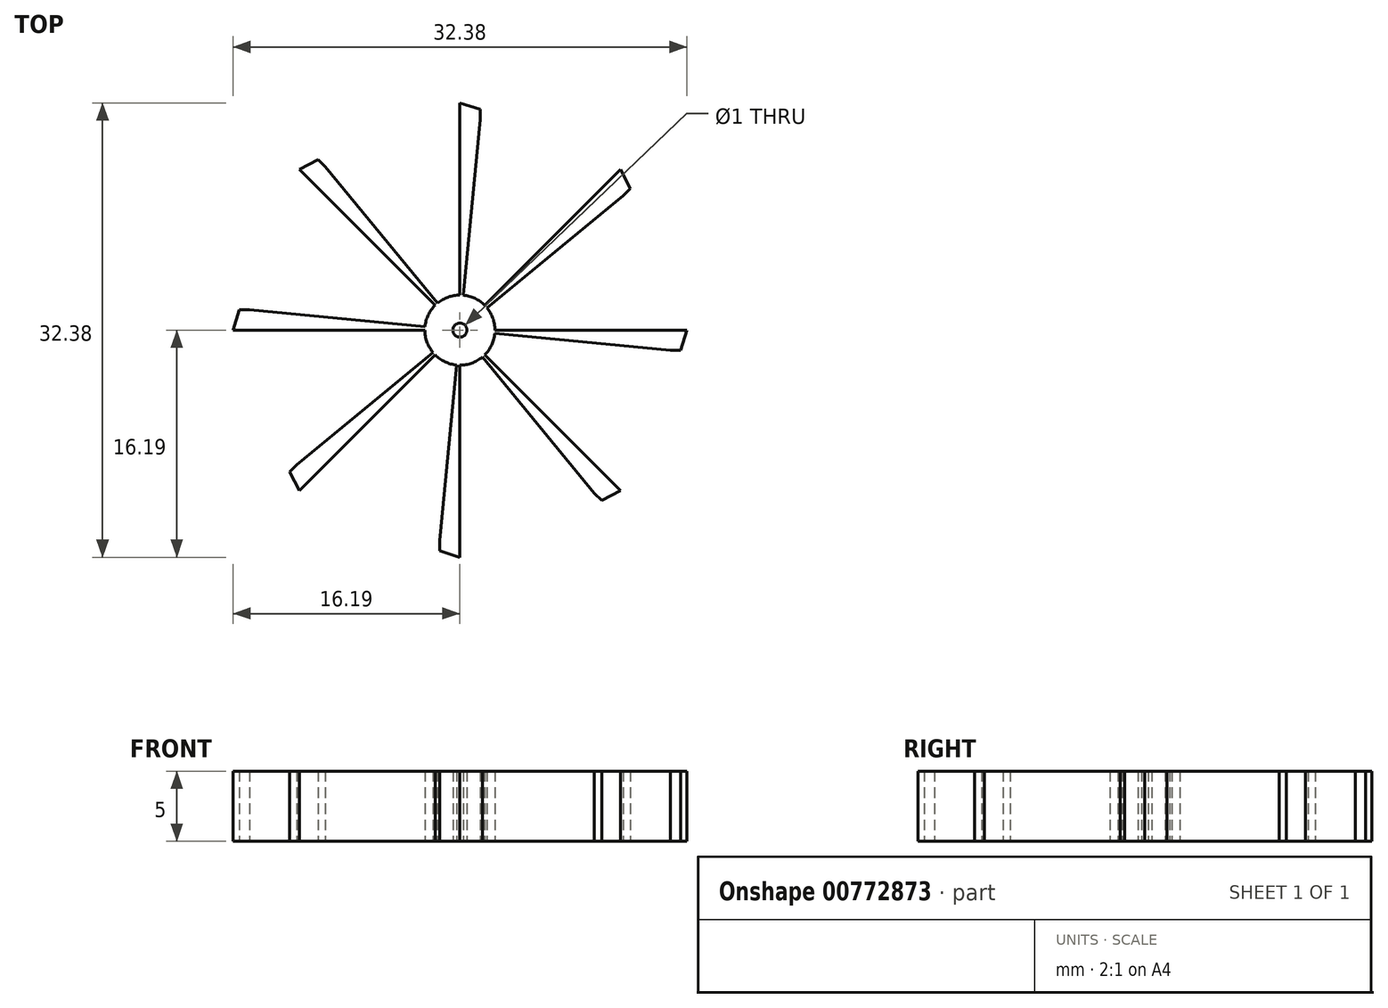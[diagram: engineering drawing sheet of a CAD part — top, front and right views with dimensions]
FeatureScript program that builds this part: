
annotation { "Feature Type Name" : "Feature", "Feature Type Description" : "" }
export const myFeature = defineFeature(function(context is Context, id is Id, definition is map)
    precondition{}
    {
        {
            var Q0;
            Q0=qCreatedBy(makeId("Top.planeOp"),FACE);
            var sketch = newSketch(context, id + "F0", { "sketchPlane" : qUnion([Q0])});
            skCircle(sketch, "E0", {"center": v(0, 0) * mm, "radius": 0.5 * mm});
            skCircle(sketch, "E1", {"center": v(0, 0) * mm, "radius": 2.5 * mm});
            skSolve(sketch);
        }
        {
            var Q0;
            Q0=makeQuery(id+"F0.imprint","IMPRINT",FACE,{"disambiguationData":[TD([[makeQuery(id+"F0.imprint","IMPRINT",EDGE,{"derivedFrom":sQuery(id+"F0.wireOp",EDGE,"E0")}),-1.0]])]});
            extrude(context, id + "F1", {"entities" : qUnion([Q0]), "depth" : 5 * mm, "offsetDistance" : 25 * mm});
        }
        {
            var Q0;
            Q0=qCreatedBy(makeId("Top.planeOp"),FACE);
            var sketch = newSketch(context, id + "F2", { "sketchPlane" : qUnion([Q0])});
            skLineSegment(sketch, "E2", {"start": v(0, 1.39) * mm, "end": v(0, 15) * mm});
            skLineSegment(sketch, "E3", {"start": v(0, 15) * mm, "end": v(1.44, 15) * mm, "construction": true});
            skLineSegment(sketch, "E4", {"start": v(1.44, 15) * mm, "end": v(0.13, 1.38) * mm});
            skLineSegment(sketch, "E5", {"start": v(0, 15) * mm, "end": v(0, 16.19) * mm});
            skLineSegment(sketch, "E6", {"start": v(0, 16.19) * mm, "end": v(1.44, 15.73) * mm});
            skLineSegment(sketch, "E7", {"start": v(1.44, 15.73) * mm, "end": v(1.44, 15) * mm});
            skLineSegment(sketch, "E8.1.0", {"start": v(-9.59, 11.63) * mm, "end": v(-0.88, 1.07) * mm});
            skLineSegment(sketch, "E8.1.1", {"start": v(-10.1, 12.14) * mm, "end": v(-9.59, 11.63) * mm});
            skLineSegment(sketch, "E8.1.2", {"start": v(-11.45, 11.45) * mm, "end": v(-10.1, 12.14) * mm});
            skLineSegment(sketch, "E8.1.3", {"start": v(-10.6, 10.6) * mm, "end": v(-11.45, 11.45) * mm});
            skLineSegment(sketch, "E8.1.4", {"start": v(-0.98, 0.98) * mm, "end": v(-10.6, 10.6) * mm});
            skLineSegment(sketch, "E8.2.0", {"start": v(-15, 1.44) * mm, "end": v(-1.38, 0.13) * mm});
            skLineSegment(sketch, "E8.2.1", {"start": v(-15.73, 1.44) * mm, "end": v(-15, 1.44) * mm});
            skLineSegment(sketch, "E8.2.2", {"start": v(-16.19, 0) * mm, "end": v(-15.73, 1.44) * mm});
            skLineSegment(sketch, "E8.2.3", {"start": v(-15, 0) * mm, "end": v(-16.19, 0) * mm});
            skLineSegment(sketch, "E8.2.4", {"start": v(-1.39, 0) * mm, "end": v(-15, 0) * mm});
            skLineSegment(sketch, "E8.3.0", {"start": v(-11.63, -9.59) * mm, "end": v(-1.07, -0.88) * mm});
            skLineSegment(sketch, "E8.3.1", {"start": v(-12.14, -10.1) * mm, "end": v(-11.63, -9.59) * mm});
            skLineSegment(sketch, "E8.3.2", {"start": v(-11.45, -11.45) * mm, "end": v(-12.14, -10.1) * mm});
            skLineSegment(sketch, "E8.3.3", {"start": v(-10.6, -10.6) * mm, "end": v(-11.45, -11.45) * mm});
            skLineSegment(sketch, "E8.3.4", {"start": v(-0.98, -0.98) * mm, "end": v(-10.6, -10.6) * mm});
            skLineSegment(sketch, "E8.4.0", {"start": v(-1.44, -15) * mm, "end": v(-0.13, -1.38) * mm});
            skLineSegment(sketch, "E8.4.1", {"start": v(-1.44, -15.73) * mm, "end": v(-1.44, -15) * mm});
            skLineSegment(sketch, "E8.4.2", {"start": v(0, -16.19) * mm, "end": v(-1.44, -15.73) * mm});
            skLineSegment(sketch, "E8.4.3", {"start": v(0, -15) * mm, "end": v(0, -16.19) * mm});
            skLineSegment(sketch, "E8.4.4", {"start": v(0, -1.39) * mm, "end": v(0, -15) * mm});
            skLineSegment(sketch, "E8.5.0", {"start": v(9.59, -11.63) * mm, "end": v(0.88, -1.07) * mm});
            skLineSegment(sketch, "E8.5.1", {"start": v(10.1, -12.14) * mm, "end": v(9.59, -11.63) * mm});
            skLineSegment(sketch, "E8.5.2", {"start": v(11.45, -11.45) * mm, "end": v(10.1, -12.14) * mm});
            skLineSegment(sketch, "E8.5.3", {"start": v(10.6, -10.6) * mm, "end": v(11.45, -11.45) * mm});
            skLineSegment(sketch, "E8.5.4", {"start": v(0.98, -0.98) * mm, "end": v(10.6, -10.6) * mm});
            skLineSegment(sketch, "E8.6.0", {"start": v(15, -1.44) * mm, "end": v(1.38, -0.13) * mm});
            skLineSegment(sketch, "E8.6.1", {"start": v(15.73, -1.44) * mm, "end": v(15, -1.44) * mm});
            skLineSegment(sketch, "E8.6.2", {"start": v(16.19, 0) * mm, "end": v(15.73, -1.44) * mm});
            skLineSegment(sketch, "E8.6.3", {"start": v(15, 0) * mm, "end": v(16.19, 0) * mm});
            skLineSegment(sketch, "E8.6.4", {"start": v(1.39, 0) * mm, "end": v(15, 0) * mm});
            skLineSegment(sketch, "E8.7.0", {"start": v(11.63, 9.59) * mm, "end": v(1.07, 0.88) * mm});
            skLineSegment(sketch, "E8.7.1", {"start": v(12.14, 10.1) * mm, "end": v(11.63, 9.59) * mm});
            skLineSegment(sketch, "E8.7.2", {"start": v(11.45, 11.45) * mm, "end": v(12.14, 10.1) * mm});
            skLineSegment(sketch, "E8.7.3", {"start": v(10.6, 10.6) * mm, "end": v(11.45, 11.45) * mm});
            skLineSegment(sketch, "E8.7.4", {"start": v(0.98, 0.98) * mm, "end": v(10.6, 10.6) * mm});
            skPoint(sketch, "E8.center", {"position": v(0, 0) * mm});
            skCircle(sketch, "E9", {"center": v(0, 0) * mm, "radius": 1.39 * mm});
            skSolve(sketch);
        }
        {
            var Q0;
            {var subQ0=sQuery(id+"F2.wireOp",EDGE,"E8.1.0");Q0=makeQuery(id+"F2.imprint","IMPRINT",FACE,{"disambiguationData":[TD([[makeQuery(id+"F2.imprint","IMPRINT",EDGE,{"derivedFrom":subQ0}),-1.0]])]});}
            var Q1;
            {var subQ1=sQuery(id+"F2.wireOp",EDGE,"E2");Q1=makeQuery(id+"F2.imprint","IMPRINT",FACE,{"disambiguationData":[TD([[makeQuery(id+"F2.imprint","IMPRINT",EDGE,{"derivedFrom":subQ1}),-1.0]])]});}
            var Q2;
            {var subQ0=sQuery(id+"F2.wireOp",EDGE,"E8.7.0");Q2=makeQuery(id+"F2.imprint","IMPRINT",FACE,{"disambiguationData":[TD([[makeQuery(id+"F2.imprint","IMPRINT",EDGE,{"derivedFrom":subQ0}),-1.0]])]});}
            var Q3;
            {var subQ1=sQuery(id+"F2.wireOp",EDGE,"E8.6.0");Q3=makeQuery(id+"F2.imprint","IMPRINT",FACE,{"disambiguationData":[TD([[makeQuery(id+"F2.imprint","IMPRINT",EDGE,{"derivedFrom":subQ1}),-1.0]])]});}
            var Q4;
            {var subQ0=sQuery(id+"F2.wireOp",EDGE,"E8.5.0");Q4=makeQuery(id+"F2.imprint","IMPRINT",FACE,{"disambiguationData":[TD([[makeQuery(id+"F2.imprint","IMPRINT",EDGE,{"derivedFrom":subQ0}),-1.0]])]});}
            var Q5;
            {var subQ0=sQuery(id+"F2.wireOp",EDGE,"E8.4.0");Q5=makeQuery(id+"F2.imprint","IMPRINT",FACE,{"disambiguationData":[TD([[makeQuery(id+"F2.imprint","IMPRINT",EDGE,{"derivedFrom":subQ0}),-1.0]])]});}
            var Q6;
            {var subQ1=sQuery(id+"F2.wireOp",EDGE,"E8.3.0");Q6=makeQuery(id+"F2.imprint","IMPRINT",FACE,{"disambiguationData":[TD([[makeQuery(id+"F2.imprint","IMPRINT",EDGE,{"derivedFrom":subQ1}),-1.0]])]});}
            var Q7;
            {var subQ0=sQuery(id+"F2.wireOp",EDGE,"E8.2.0");Q7=makeQuery(id+"F2.imprint","IMPRINT",FACE,{"disambiguationData":[TD([[makeQuery(id+"F2.imprint","IMPRINT",EDGE,{"derivedFrom":subQ0}),-1.0]])]});}
            extrude(context, id + "F3", {"entities" : qUnion([Q0, Q1, Q2, Q3, Q4, Q5, Q6, Q7]), "operationType" : NewBodyOperationType.ADD, "depth" : 5 * mm, "offsetDistance" : 25 * mm});
        }
    });
